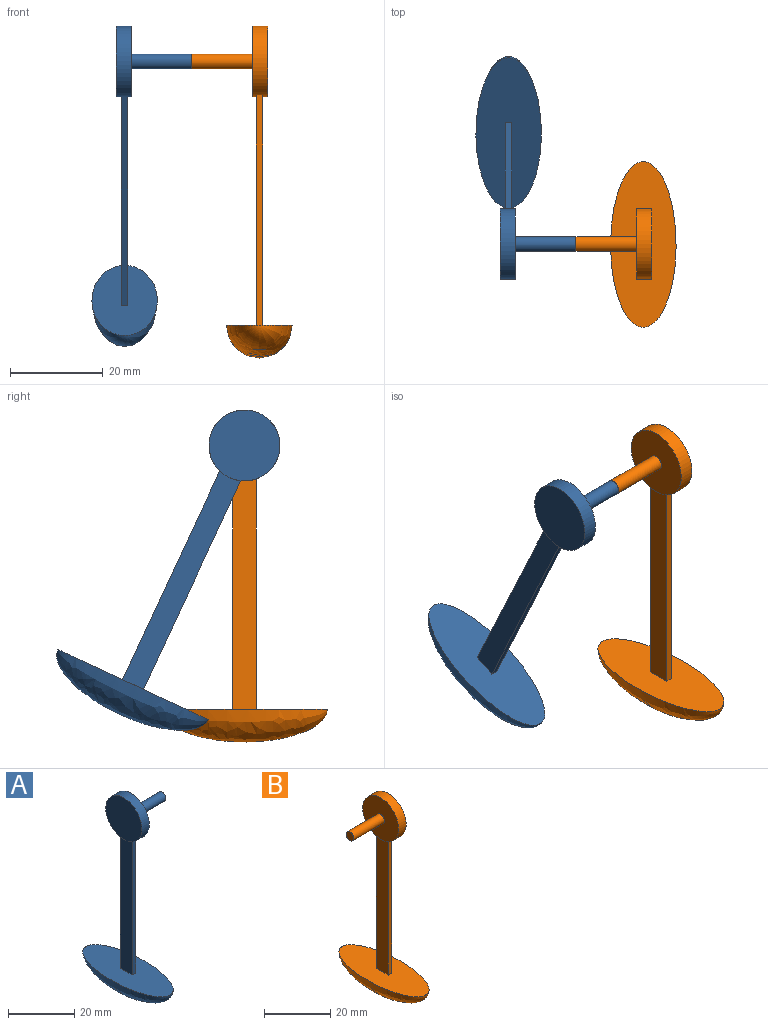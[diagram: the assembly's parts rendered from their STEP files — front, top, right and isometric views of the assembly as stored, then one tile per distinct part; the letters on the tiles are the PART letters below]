
ASSEMBLY  parts=2 mates=1
PART A: 11 faces, bbox 21.6x35.8x71.8 mm
  f0: plane 3.21x3.21mm, normal (1,0,0), area 8.1mm2, adj f1
  f1: cylinder r=1.6mm len=13.11mm, axis (-1,0,0), area 132.1mm2, adj f0,f2
  f2: plane 15.32x15.32mm, normal (1,0,0), area 176.4mm2, adj f1,f3
  f3: cylinder r=7.66mm len=15.32mm, axis (-1,0,0), area 149.3mm2, adj f2,f4,f5,f6,f7,f8
  f4: plane 15.32x15.32mm, normal (-1,0,0), area 184.4mm2, adj f3
  f5: plane 49.78x1.43mm, normal (0,-1,0), area 71mm2, adj f3,f7,f8,f9
  f6: plane 49.78x1.43mm, normal (0,1,0), area 71mm2, adj f3,f7,f8,f9
  f7: plane 49.78x5mm, normal (1,0,0), area 247.5mm2, adj f3,f5,f6,f9
  f8: plane 49.78x5mm, normal (-1,0,0), area 247.5mm2, adj f3,f5,f6,f9
  f9: plane 35.82x14.18mm, normal (0,0,1), area 391.9mm2, adj f5,f6,f7,f8,f10
  f10: revolved ~35.82x14.18mm, area 663.8mm2, adj f9
PART B: 11 faces, bbox 21.6x35.8x71.8 mm
  f0: plane 3.21x3.21mm, normal (-1,0,0), area 8.1mm2, adj f1
  f1: cylinder r=1.6mm len=13.11mm, axis (1,0,0), area 132.1mm2, adj f0,f2
  f2: plane 15.32x15.32mm, normal (-1,0,0), area 176.4mm2, adj f1,f3
  f3: cylinder r=7.66mm len=15.32mm, axis (1,0,0), area 149.3mm2, adj f2,f4,f5,f6,f7,f8
  f4: plane 15.32x15.32mm, normal (1,0,0), area 184.4mm2, adj f3
  f5: plane 49.78x1.43mm, normal (0,-1,0), area 71mm2, adj f3,f7,f8,f9
  f6: plane 49.78x1.43mm, normal (0,1,0), area 71mm2, adj f3,f7,f8,f9
  f7: plane 49.78x5mm, normal (-1,0,0), area 247.5mm2, adj f3,f5,f6,f9
  f8: plane 49.78x5mm, normal (1,0,0), area 247.5mm2, adj f3,f5,f6,f9
  f9: plane 35.82x14.18mm, normal (0,0,1), area 391.9mm2, adj f5,f6,f7,f8,f10
  f10: revolved ~35.82x14.18mm, area 663.8mm2, adj f9
PLACE A rot(axis=(1,0,0),25deg) t=(18.36,42.09,-35.32)mm
PLACE B t=(18.36,14.27,-41.49)mm
MATE revolute A.f1 <-> B.f1  axis (1,0,0) through (18.36,14.27,24.36)mm
